# Revit family: Sphere_High Back_Depth adjustment Seat_Fixed Arm_Hollow Caster_CTK8SC
name_source: partatom
category: Furniture
units: mm (PartAtom-declared; Revit-internal decimal feet)

## family parameters
Always vertical = Yes
Cut with Voids When Loaded = No
OmniClass Number = 23.40.20.00
OmniClass Title = General Furniture and Specialties
Room Calculation Point = No
Shared = No
Work Plane-Based = No

## types (7) — shared parameters
Assembly Code = E2020200
D = 24.4 "
H = 42 "
Keynote = 12490
Manufacturer = 株式会社オカムラ
URL = http://www.okamura.co.jp
W = 25.5 "
キャスター = okm_G155
ボディ・脚 = okm_G721
他 = okm_G721
区分 = チェア
品番 = CT2AFA
支柱 = okm_silver FX4
肘パッド = okm_G721
製品カテゴリ = オフィスシーティング

## per-type parameters (varying)
| type | 張材_表側 | 張材_裏側 |
| FRU2（ダークグレー） | okm_FRU2 | okm_FRU1 |
| FRU1（ブラック） | okm_FRU1 | okm_FRU1 |
| FRU4（ダークブルー） | okm_FRU4 | okm_FRU1 |
| FRU5（ダークグリーン） | okm_FRU5 | okm_FRU1 |
| FXW0（ダークグレー） | okm_FXW0 | okm_FXW0 |
| FXW4（インディゴ） | okm_FXW4 | okm_FXW0 |
| FXW5（ダークグリーン） | okm_FXW5 | okm_FXW0 |
